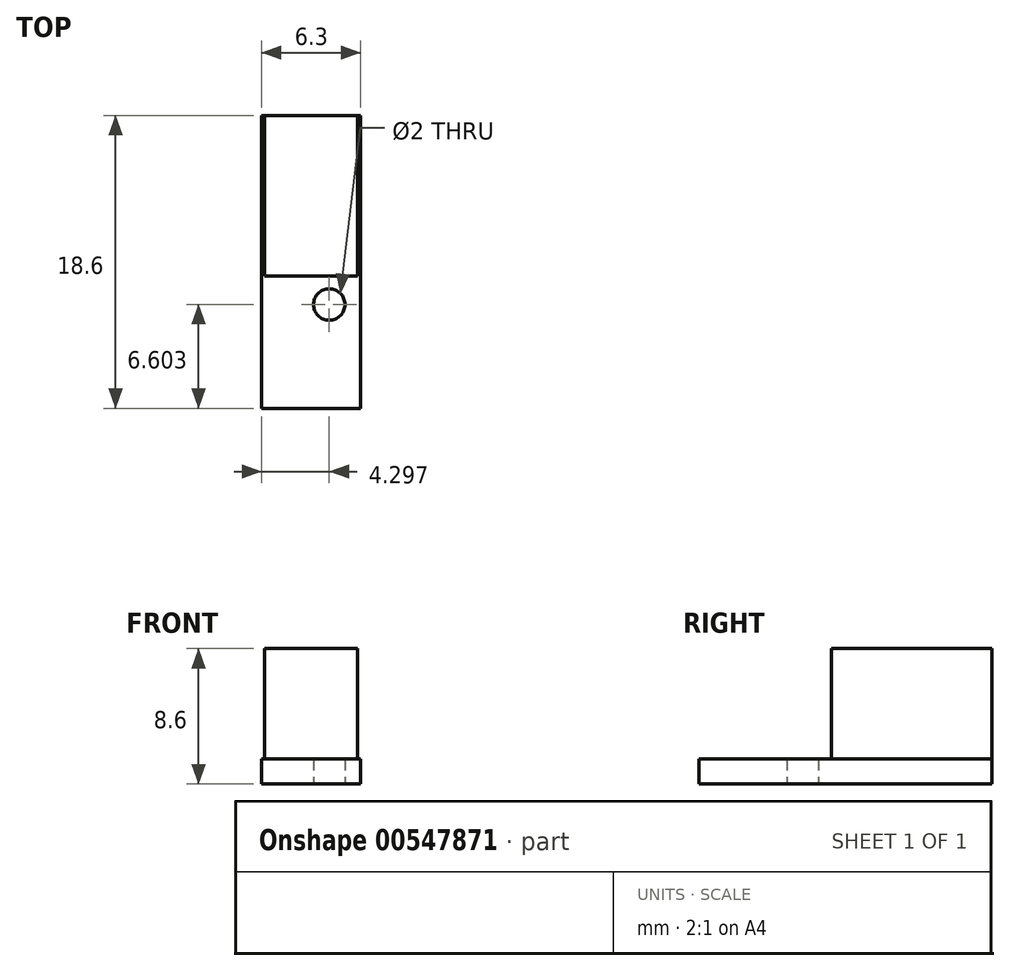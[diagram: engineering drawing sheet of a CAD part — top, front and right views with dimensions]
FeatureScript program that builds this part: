
annotation { "Feature Type Name" : "Feature", "Feature Type Description" : "" }
export const myFeature = defineFeature(function(context is Context, id is Id, definition is map)
    precondition{}
    {
        {
            var Q0;
            Q0=qCreatedBy(makeId("Top.planeOp"),FACE);
            var sketch = newSketch(context, id + "F0", { "sketchPlane" : qUnion([Q0])});
            skLineSegment(sketch, "E0.bottom", {"start": v(-28.45, 14.75) * mm, "end": v(-22.15, 14.75) * mm});
            skLineSegment(sketch, "E0.top", {"start": v(-28.45, -3.85) * mm, "end": v(-22.15, -3.85) * mm});
            skLineSegment(sketch, "E0.left", {"start": v(-28.45, 14.75) * mm, "end": v(-28.45, -3.85) * mm});
            skLineSegment(sketch, "E0.right", {"start": v(-22.15, 14.75) * mm, "end": v(-22.15, -3.85) * mm});
            skCircle(sketch, "E1", {"center": v(-24.15, 2.75) * mm, "radius": 1 * mm});
            skSolve(sketch);
        }
        {
            var Q0;
            Q0=makeQuery(id+"F0.imprint","IMPRINT",FACE,{"disambiguationData":[TD([[makeQuery(id+"F0.imprint","IMPRINT",EDGE,{"derivedFrom":sQuery(id+"F0.wireOp",EDGE,"E0.bottom")}),-1.0]])]});
            extrude(context, id + "F1", {"entities" : qUnion([Q0]), "depth" : 1.6 * mm, "offsetDistance" : 25 * mm});
        }
        {
            var Q0;
            Q0=makeQuery(id+"F1.opExtrude","CAP_FACE",FACE,{"disambiguationData":[OSD([sQuery(id+"F0.wireOp",EDGE,"E0.bottom"),sQuery(id+"F0.wireOp",EDGE,"E0.top"),sQuery(id+"F0.wireOp",EDGE,"E0.left"),sQuery(id+"F0.wireOp",EDGE,"E0.right")])],"isStart":false});
            var sketch = newSketch(context, id + "F2", { "sketchPlane" : qUnion([Q0])});
            skLineSegment(sketch, "E2.bottom", {"start": v(-28.25, 14.75) * mm, "end": v(-22.35, 14.75) * mm});
            skLineSegment(sketch, "E2.top", {"start": v(-28.25, 4.55) * mm, "end": v(-22.35, 4.55) * mm});
            skLineSegment(sketch, "E2.left", {"start": v(-28.25, 14.75) * mm, "end": v(-28.25, 4.55) * mm});
            skLineSegment(sketch, "E2.right", {"start": v(-22.35, 14.75) * mm, "end": v(-22.35, 4.55) * mm});
            skLineSegment(sketch, "E3", {"start": v(-25.3, 4.55) * mm, "end": v(-25.3, -3.85) * mm, "construction": true});
            skSolve(sketch);
        }
        {
            var Q0;
            Q0=makeQuery(id+"F2.imprint","IMPRINT",FACE,{"disambiguationData":[TD([[makeQuery(id+"F2.imprint","IMPRINT",EDGE,{"derivedFrom":sQuery(id+"F2.wireOp",EDGE,"E2.bottom")}),-1.0]])]});
            extrude(context, id + "F3", {"entities" : qUnion([Q0]), "operationType" : NewBodyOperationType.ADD, "depth" : 7 * mm, "offsetDistance" : 25 * mm});
        }
    });
